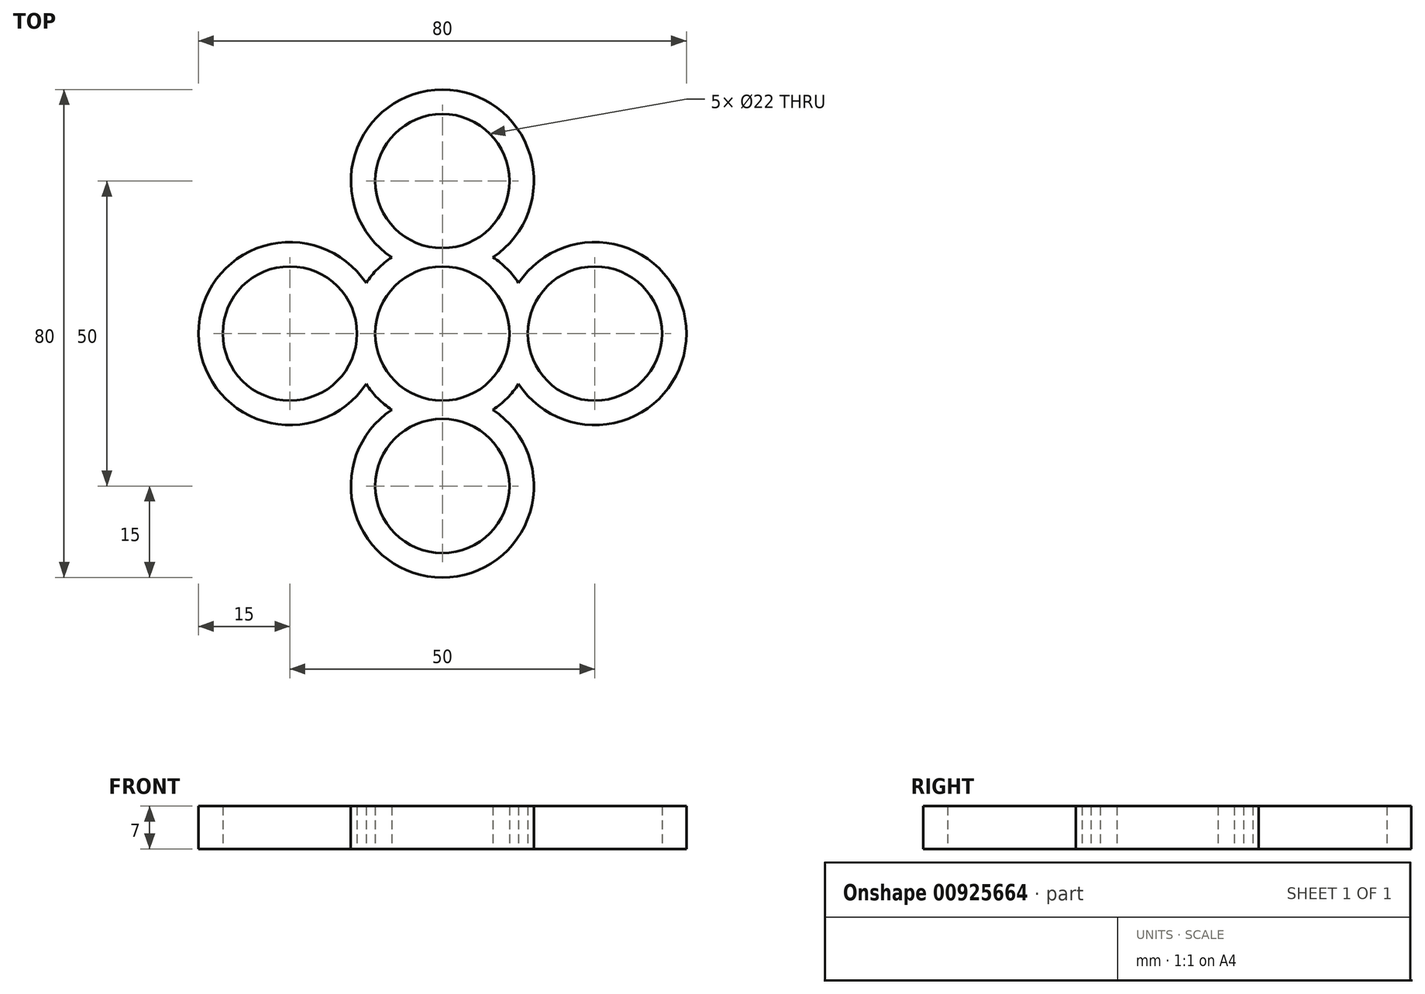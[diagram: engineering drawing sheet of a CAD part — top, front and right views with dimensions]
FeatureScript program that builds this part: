
annotation { "Feature Type Name" : "Feature", "Feature Type Description" : "" }
export const myFeature = defineFeature(function(context is Context, id is Id, definition is map)
    precondition{}
    {
        {
            var Q0;
            Q0=qCreatedBy(makeId("Top.planeOp"),FACE);
            var sketch = newSketch(context, id + "F0", { "sketchPlane" : qUnion([Q0])});
            skArc(sketch, "E0", {"start": v(7.78, 7.78) * mm, "mid": v(0, 11) * mm, "end": v(-7.78, 7.78) * mm});
            skCircle(sketch, "E1", {"center": v(0, 25) * mm, "radius": 11 * mm});
            skArc(sketch, "E2", {"start": v(8.3, 12.5) * mm, "mid": v(0, 40) * mm, "end": v(-8.3, 12.5) * mm});
            skArc(sketch, "E3", {"start": v(-8.3, 12.5) * mm, "mid": v(-9.5, 11.61) * mm, "end": v(-10.6, 10.6) * mm});
            skArc(sketch, "E4.trimOffspring", {"start": v(10.6, 10.6) * mm, "mid": v(9.5, 11.61) * mm, "end": v(8.3, 12.5) * mm});
            skCircle(sketch, "E5.1.0", {"center": v(-25, 0) * mm, "radius": 11 * mm});
            skArc(sketch, "E5.1.1", {"start": v(-12.5, 8.3) * mm, "mid": v(-40, 0) * mm, "end": v(-12.5, -8.3) * mm});
            skArc(sketch, "E5.1.2", {"start": v(-7.78, 7.78) * mm, "mid": v(-11, 0) * mm, "end": v(-7.78, -7.78) * mm});
            skArc(sketch, "E5.1.3", {"start": v(-12.5, -8.3) * mm, "mid": v(-11.61, -9.5) * mm, "end": v(-10.6, -10.6) * mm});
            skArc(sketch, "E5.1.4", {"start": v(-10.6, 10.6) * mm, "mid": v(-11.61, 9.5) * mm, "end": v(-12.5, 8.3) * mm});
            skCircle(sketch, "E5.2.0", {"center": v(0, -25) * mm, "radius": 11 * mm});
            skArc(sketch, "E5.2.1", {"start": v(-8.3, -12.5) * mm, "mid": v(0, -40) * mm, "end": v(8.3, -12.5) * mm});
            skArc(sketch, "E5.2.2", {"start": v(-7.78, -7.78) * mm, "mid": v(0, -11) * mm, "end": v(7.78, -7.78) * mm});
            skArc(sketch, "E5.2.3", {"start": v(8.3, -12.5) * mm, "mid": v(9.5, -11.61) * mm, "end": v(10.6, -10.6) * mm});
            skArc(sketch, "E5.2.4", {"start": v(-10.6, -10.6) * mm, "mid": v(-9.5, -11.61) * mm, "end": v(-8.3, -12.5) * mm});
            skCircle(sketch, "E5.3.0", {"center": v(25, 0) * mm, "radius": 11 * mm});
            skArc(sketch, "E5.3.1", {"start": v(12.5, -8.3) * mm, "mid": v(40, 0) * mm, "end": v(12.5, 8.3) * mm});
            skArc(sketch, "E5.3.2", {"start": v(7.78, -7.78) * mm, "mid": v(11, 0) * mm, "end": v(7.78, 7.78) * mm});
            skArc(sketch, "E5.3.3", {"start": v(12.5, 8.3) * mm, "mid": v(11.61, 9.5) * mm, "end": v(10.6, 10.6) * mm});
            skArc(sketch, "E5.3.4", {"start": v(10.6, -10.6) * mm, "mid": v(11.61, -9.5) * mm, "end": v(12.5, -8.3) * mm});
            skSolve(sketch);
        }
        {
            var Q0;
            Q0 = qSketchRegion(id + "F0", true);
            extrude(context, id + "F1", {"entities" : qUnion([Q0]), "depth" : 7 * mm, "offsetDistance" : 25 * mm});
        }
    });
